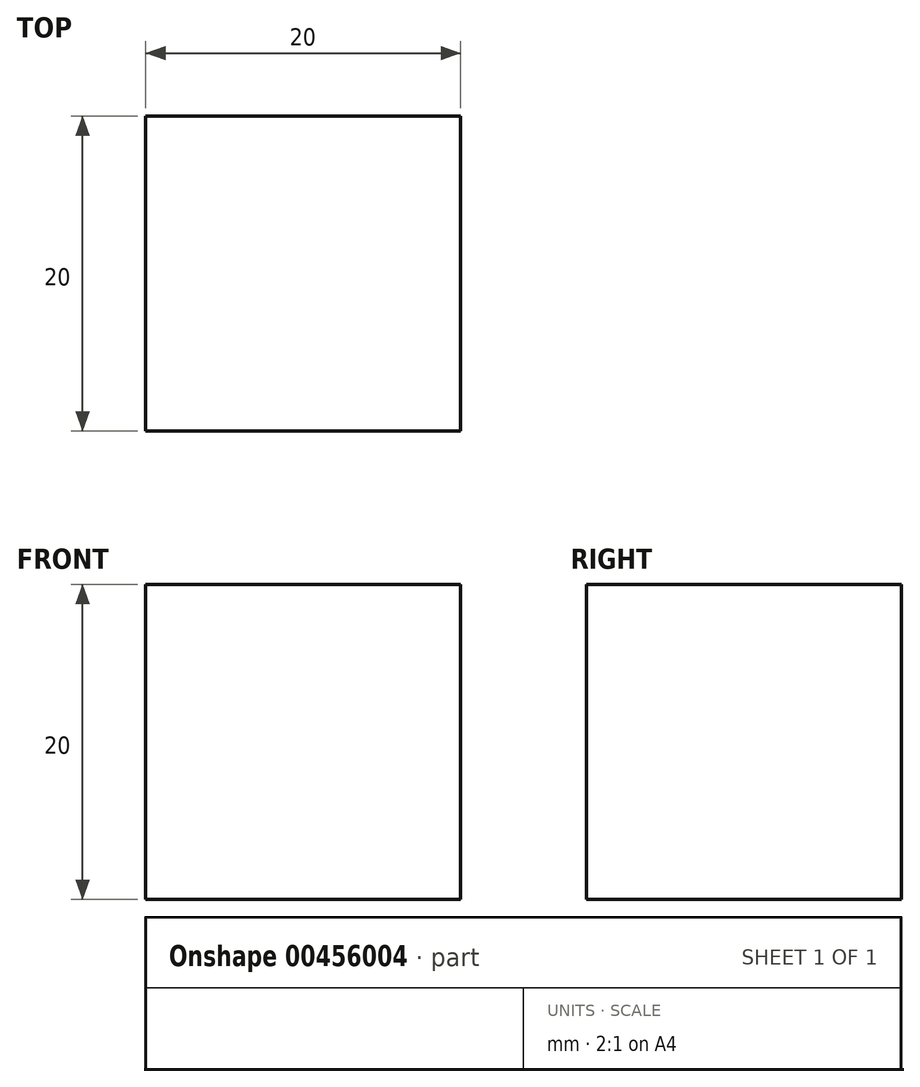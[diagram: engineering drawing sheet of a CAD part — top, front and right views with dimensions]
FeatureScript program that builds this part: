
annotation { "Feature Type Name" : "Feature", "Feature Type Description" : "" }
export const myFeature = defineFeature(function(context is Context, id is Id, definition is map)
    precondition{}
    {
        {
            var Q0;
            Q0=qCreatedBy(makeId("Front.planeOp"),FACE);
            var sketch = newSketch(context, id + "F0", { "sketchPlane" : qUnion([Q0])});
            skLineSegment(sketch, "E0.bottom", {"start": v(-20, 20) * mm, "end": v(0, 20) * mm});
            skLineSegment(sketch, "E0.top", {"start": v(-20, 0) * mm, "end": v(0, 0) * mm});
            skLineSegment(sketch, "E0.left", {"start": v(-20, 20) * mm, "end": v(-20, 0) * mm});
            skLineSegment(sketch, "E0.right", {"start": v(0, 20) * mm, "end": v(0, 0) * mm});
            skSolve(sketch);
        }
        {
            var Q0;
            Q0 = qSketchRegion(id + "F0", true);
            extrude(context, id + "F1", {"entities" : qUnion([Q0]), "depth" : 20 * mm});
        }
    });
